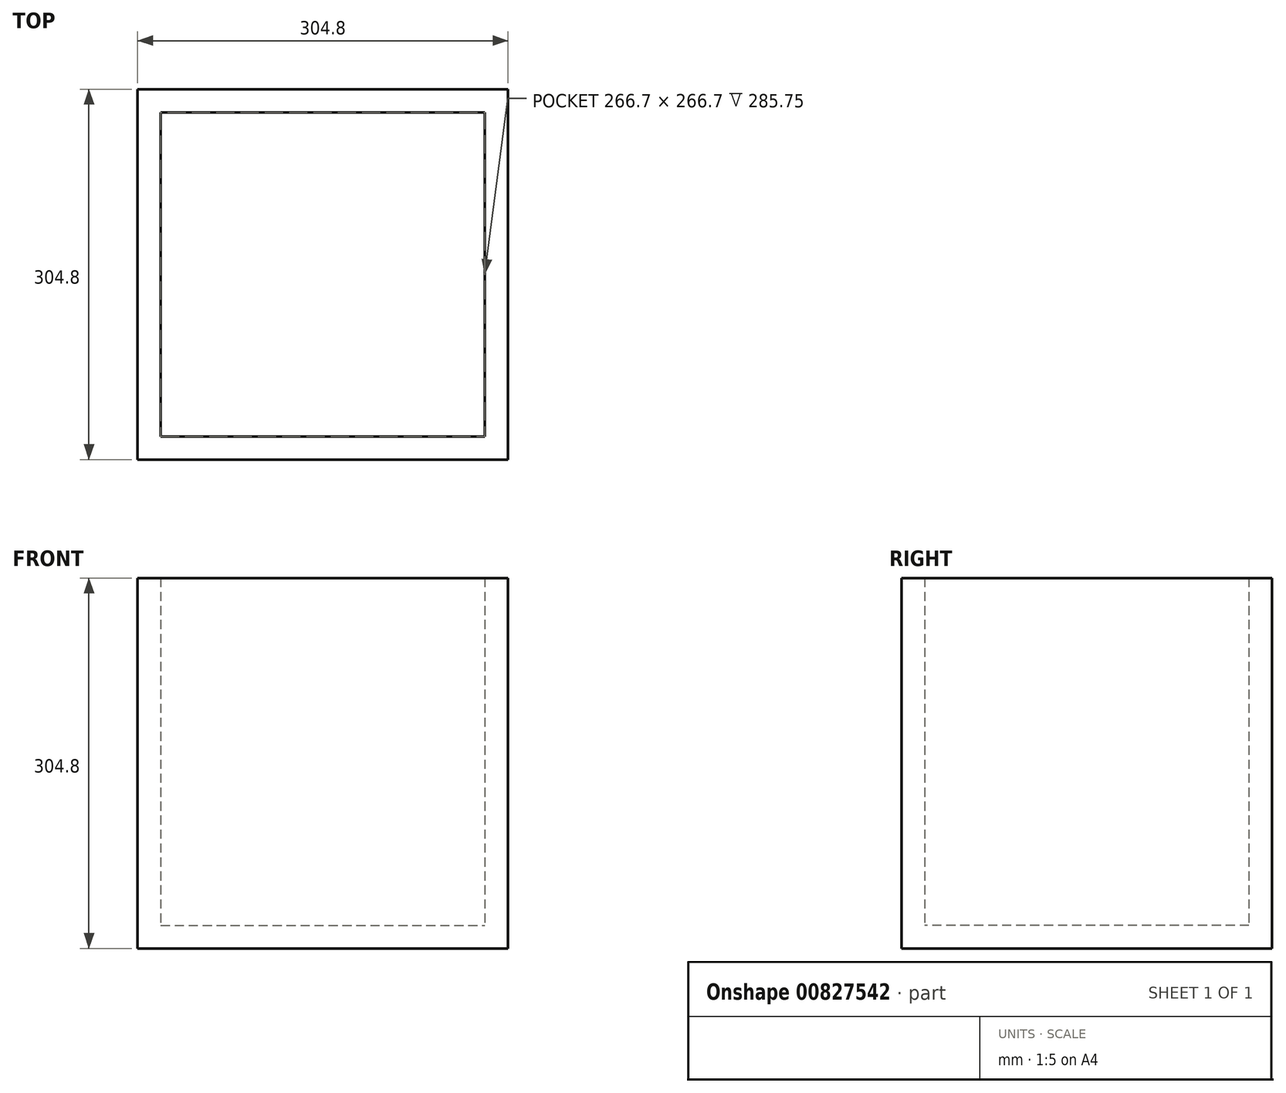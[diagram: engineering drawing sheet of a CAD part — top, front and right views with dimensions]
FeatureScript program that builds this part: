
annotation { "Feature Type Name" : "Feature", "Feature Type Description" : "" }
export const myFeature = defineFeature(function(context is Context, id is Id, definition is map)
    precondition{}
    {
        {
            var Q0;
            Q0=qCreatedBy(makeId("Top.planeOp"),FACE);
            var sketch = newSketch(context, id + "F0", { "sketchPlane" : qUnion([Q0])});
            skLineSegment(sketch, "E0.bottom", {"start": v(-152.4, 152.4) * mm, "end": v(152.4, 152.4) * mm});
            skLineSegment(sketch, "E0.top", {"start": v(-152.4, -152.4) * mm, "end": v(152.4, -152.4) * mm});
            skLineSegment(sketch, "E0.left", {"start": v(-152.4, 152.4) * mm, "end": v(-152.4, -152.4) * mm});
            skLineSegment(sketch, "E0.right", {"start": v(152.4, 152.4) * mm, "end": v(152.4, -152.4) * mm});
            skPoint(sketch, "E0.middle", {"position": v(0, 0) * mm});
            skSolve(sketch);
        }
        {
            var Q0;
            Q0=makeQuery(id+"F0.imprint","IMPRINT",FACE,{"disambiguationData":[TD([[makeQuery(id+"F0.imprint","IMPRINT",EDGE,{"derivedFrom":sQuery(id+"F0.wireOp",EDGE,"E0.bottom")}),-1.0]])]});
            extrude(context, id + "F1", {"entities" : qUnion([Q0]), "depth" : 304.8 * mm, "offsetDistance" : 25.4 * mm, "symmetric" : true});
        }
        {
            var Q0;
            Q0=makeQuery(id+"F1.opExtrude","CAP_FACE",FACE,{"disambiguationData":[OSD([sQuery(id+"F0.wireOp",EDGE,"E0.bottom"),sQuery(id+"F0.wireOp",EDGE,"E0.top"),sQuery(id+"F0.wireOp",EDGE,"E0.left"),sQuery(id+"F0.wireOp",EDGE,"E0.right")])],"isStart":false});
            shell(context, id + "F2", {"entities" : qUnion([Q0]), "thickness" : 19.05 * mm});
        }
    });
